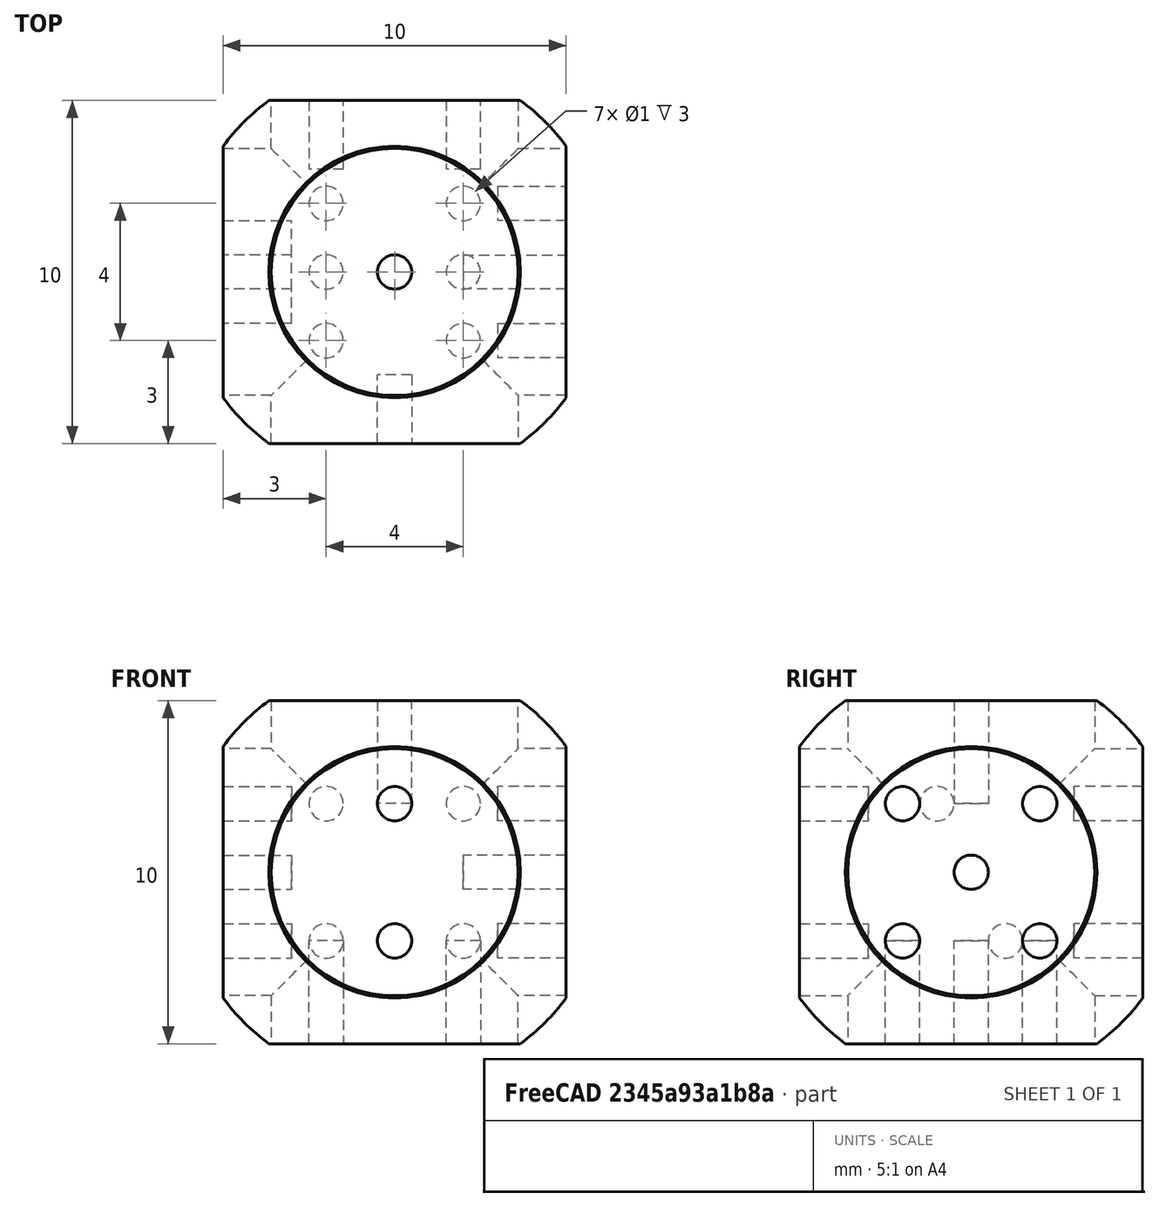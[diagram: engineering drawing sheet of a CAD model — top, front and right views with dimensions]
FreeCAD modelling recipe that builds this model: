
FCSTD DOCUMENT  (FreeCAD 0.21R33694 (Git))
Label: gcasna_repte_exercici02_Robo2
License: All rights reserved
LicenseURL: http://en.wikipedia.org/wiki/All_rights_reserved
objects: Part::Cylinder×24, Part::MultiFuse×6, Part::Cut×6, Part::Box×1, Part::Sphere×1, Part::Fillet×1, Part::MultiCommon×1
note: 40 computed .brp shape members not serialized (recipe doc carries the construction recipe); baked Part::Feature solids carry a one-line shape summary decoded from their .brp

FEATURE [Part::Box] Box  label="Cube"
  AttacherType = Attacher::AttachEngine3D
  Height = 10
  Length = 10
  Placement = pos=(-5,-6,-4) rot=(0,0,1;0rad)
  Width = 10
FEATURE [Part::Sphere] Sphere
  Angle1 = -90
  Angle2 = 90
  Angle3 = 360
  AttacherType = Attacher::AttachEngine3D
  Placement = pos=(0,0,1) rot=(0,0,1;0rad)
  Radius = 6.2
FEATURE [Part::Fillet] Fillet
  Base = -> Box
  Edges = 9 edges r=1: [Edge1,Edge2,Edge5,Edge6,Edge7,Edge8,Edge9,Edge10,Edge12]
  Placement = pos=(0,1,0) rot=(0,0,1;0rad)
FEATURE [Part::MultiCommon] Common
  Refine = true
  Shapes = -> [Sphere,Fillet]
FEATURE [Part::Cylinder] Cylinder
  Angle = 360
  AttacherType = Attacher::AttachEngine3D
  FirstAngle = 0
  Height = 10
  Placement = pos=(0,0,-4) rot=(0,0,1;0rad)
  Radius = 3.6
  SecondAngle = 0
FEATURE [Part::Cylinder] Cylinder001
  Angle = 360
  AttacherType = Attacher::AttachEngine3D
  FirstAngle = 0
  Height = 10
  Placement = pos=(0,5,1) rot=(1,0,0;1.5708rad)
  Radius = 3.6
  SecondAngle = 0
FEATURE [Part::Cylinder] Cylinder002
  Angle = 360
  AttacherType = Attacher::AttachEngine3D
  FirstAngle = 0
  Height = 10
  Placement = pos=(-5,0,1) rot=(0.57735,0.57735,0.57735;2.0944rad)
  Radius = 3.6
  SecondAngle = 0
FEATURE [Part::MultiFuse] Fusion
  Refine = true
  Shapes = -> [Cylinder,Cylinder001,Cylinder002]
FEATURE [Part::Cylinder] Cylinder003
  Angle = 360
  AttacherType = Attacher::AttachEngine3D
  FirstAngle = 0
  Height = 5
  Placement = pos=(0,0,3) rot=(0,0,1;0rad)
  Radius = 0.5
  SecondAngle = 0
FEATURE [Part::Cylinder] Cylinder004
  Angle = 360
  AttacherType = Attacher::AttachEngine3D
  FirstAngle = 0
  Height = 5
  Placement = pos=(0,-3,3) rot=(1,0,0;1.5708rad)
  Radius = 0.5
  SecondAngle = 0
FEATURE [Part::Cylinder] Cylinder005
  Angle = 360
  AttacherType = Attacher::AttachEngine3D
  FirstAngle = 0
  Height = 5
  Placement = pos=(0,-3,-1) rot=(1,0,0;1.5708rad)
  Radius = 0.5
  SecondAngle = 0
FEATURE [Part::Cylinder] Cylinder006
  Angle = 360
  AttacherType = Attacher::AttachEngine3D
  FirstAngle = 0
  Height = 5
  Placement = pos=(-3,-1,3) rot=(0.57735,-0.57735,-0.57735;2.0944rad)
  Radius = 0.5
  SecondAngle = 0
FEATURE [Part::Cylinder] Cylinder007
  Angle = 360
  AttacherType = Attacher::AttachEngine3D
  FirstAngle = 0
  Height = 5
  Placement = pos=(-3,0,1) rot=(0.57735,-0.57735,-0.57735;2.0944rad)
  Radius = 0.5
  SecondAngle = 0
FEATURE [Part::Cylinder] Cylinder008
  Angle = 360
  AttacherType = Attacher::AttachEngine3D
  FirstAngle = 0
  Height = 5
  Placement = pos=(-3,1,-1) rot=(0.57735,-0.57735,-0.57735;2.0944rad)
  Radius = 0.5
  SecondAngle = 0
FEATURE [Part::Cylinder] Cylinder009
  Angle = 360
  AttacherType = Attacher::AttachEngine3D
  FirstAngle = 0
  Height = 5
  Placement = pos=(3,-2,3) rot=(0.57735,0.57735,0.57735;2.0944rad)
  Radius = 0.5
  SecondAngle = 0
FEATURE [Part::Cylinder] Cylinder010
  Angle = 360
  AttacherType = Attacher::AttachEngine3D
  FirstAngle = 0
  Height = 5
  Placement = pos=(3,-2,-1) rot=(0.57735,0.57735,0.57735;2.0944rad)
  Radius = 0.5
  SecondAngle = 0
FEATURE [Part::Cylinder] Cylinder011
  Angle = 360
  AttacherType = Attacher::AttachEngine3D
  FirstAngle = 0
  Height = 5
  Placement = pos=(3,2,3) rot=(0.57735,0.57735,0.57735;2.0944rad)
  Radius = 0.5
  SecondAngle = 0
FEATURE [Part::Cylinder] Cylinder012
  Angle = 360
  AttacherType = Attacher::AttachEngine3D
  FirstAngle = 0
  Height = 5
  Placement = pos=(3,2,-1) rot=(0.57735,0.57735,0.57735;2.0944rad)
  Radius = 0.5
  SecondAngle = 0
FEATURE [Part::Cylinder] Cylinder013
  Angle = 360
  AttacherType = Attacher::AttachEngine3D
  FirstAngle = 0
  Height = 5
  Placement = pos=(2,0,1) rot=(0.57735,0.57735,0.57735;2.0944rad)
  Radius = 0.5
  SecondAngle = 0
FEATURE [Part::MultiFuse] Fusion001
  Refine = true
  Shapes = -> [Cylinder013,Cylinder012,Cylinder011,Cylinder010,Cylinder009]
FEATURE [Part::MultiFuse] Fusion002
  Refine = true
  Shapes = -> [Cylinder008,Cylinder007,Cylinder006]
FEATURE [Part::Cylinder] Cylinder014
  Angle = 360
  AttacherType = Attacher::AttachEngine3D
  FirstAngle = 0
  Height = 5
  Placement = pos=(-2,-2,-1) rot=(1,0,0;3.14159rad)
  Radius = 0.5
  SecondAngle = 0
FEATURE [Part::Cylinder] Cylinder015
  Angle = 360
  AttacherType = Attacher::AttachEngine3D
  FirstAngle = 0
  Height = 5
  Placement = pos=(-2,0,-1) rot=(1,0,0;3.14159rad)
  Radius = 0.5
  SecondAngle = 0
FEATURE [Part::Cylinder] Cylinder016
  Angle = 360
  AttacherType = Attacher::AttachEngine3D
  FirstAngle = 0
  Height = 5
  Placement = pos=(-2,2,-1) rot=(1,0,0;3.14159rad)
  Radius = 0.5
  SecondAngle = 0
FEATURE [Part::Cylinder] Cylinder017
  Angle = 360
  AttacherType = Attacher::AttachEngine3D
  FirstAngle = 0
  Height = 5
  Placement = pos=(2,2,-1) rot=(1,0,0;3.14159rad)
  Radius = 0.5
  SecondAngle = 0
FEATURE [Part::Cylinder] Cylinder018
  Angle = 360
  AttacherType = Attacher::AttachEngine3D
  FirstAngle = 0
  Height = 5
  Placement = pos=(2,0,-1) rot=(1,0,0;3.14159rad)
  Radius = 0.5
  SecondAngle = 0
FEATURE [Part::Cylinder] Cylinder019
  Angle = 360
  AttacherType = Attacher::AttachEngine3D
  FirstAngle = 0
  Height = 5
  Placement = pos=(2,-2,-1) rot=(1,0,0;3.14159rad)
  Radius = 0.5
  SecondAngle = 0
FEATURE [Part::MultiFuse] Fusion003
  Refine = true
  Shapes = -> [Cylinder014,Cylinder015,Cylinder016,Cylinder017,Cylinder018,Cylinder019]
FEATURE [Part::Cut] Cut
  Base = -> Fusion
  Refine = true
  Tool = -> Fusion001
FEATURE [Part::Cut] Cut001
  Base = -> Fusion
  Refine = true
  Tool = -> Fusion003
FEATURE [Part::Cut] Cut002
  Base = -> Fusion
  Refine = true
  Tool = -> Fusion002
FEATURE [Part::Cut] Cut003
  Base = -> Fusion
  Refine = true
  Tool = -> Cylinder003
FEATURE [Part::MultiFuse] Fusion004
  Refine = true
  Shapes = -> [Cylinder004,Cylinder005]
FEATURE [Part::Cut] Cut004
  Base = -> Fusion
  Refine = true
  Tool = -> Fusion004
FEATURE [Part::Cylinder] Cylinder020
  Angle = 360
  AttacherType = Attacher::AttachEngine3D
  FirstAngle = 0
  Height = 5
  Placement = pos=(2,3,3) rot=(-1,0,0;1.5708rad)
  Radius = 0.5
  SecondAngle = 0
FEATURE [Part::Cylinder] Cylinder021
  Angle = 360
  AttacherType = Attacher::AttachEngine3D
  FirstAngle = 0
  Height = 5
  Placement = pos=(-2,3,3) rot=(-1,0,0;1.5708rad)
  Radius = 0.5
  SecondAngle = 0
FEATURE [Part::Cylinder] Cylinder022
  Angle = 360
  AttacherType = Attacher::AttachEngine3D
  FirstAngle = 0
  Height = 5
  Placement = pos=(-2,3,-1) rot=(-1,0,0;1.5708rad)
  Radius = 0.5
  SecondAngle = 0
FEATURE [Part::Cylinder] Cylinder023
  Angle = 360
  AttacherType = Attacher::AttachEngine3D
  FirstAngle = 0
  Height = 5
  Placement = pos=(2,3,-1) rot=(-1,0,0;1.5708rad)
  Radius = 0.5
  SecondAngle = 0
FEATURE [Part::MultiFuse] Fusion005
  Refine = true
  Shapes = -> [Cylinder020,Cylinder021,Cylinder022,Cylinder023]
FEATURE [Part::Cut] Cut005
  Base = -> Fusion
  Refine = true
  Tool = -> Fusion005
